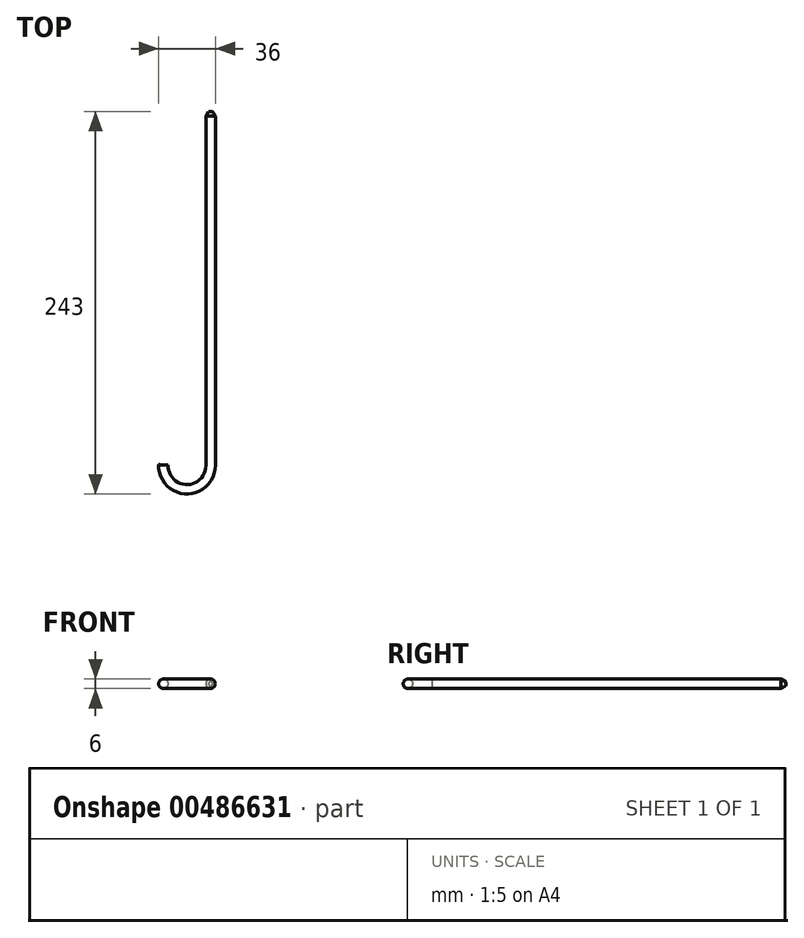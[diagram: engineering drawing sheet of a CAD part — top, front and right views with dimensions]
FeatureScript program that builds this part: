
annotation { "Feature Type Name" : "Feature", "Feature Type Description" : "" }
export const myFeature = defineFeature(function(context is Context, id is Id, definition is map)
    precondition{}
    {
        {
            var Q0;
            Q0=qCreatedBy(makeId("Top.planeOp"),FACE);
            var sketch = newSketch(context, id + "F0", { "sketchPlane" : qUnion([Q0])});
            skLineSegment(sketch, "E0", {"start": v(0, 0) * mm, "end": v(0, -225) * mm});
            skArc(sketch, "E1", {"start": v(0, -225) * mm, "mid": v(-15.28, -240) * mm, "end": v(-29.99, -224.45) * mm});
            skSolve(sketch);
        }
        {
            var Q0;
            Q0=qCreatedBy(makeId("Front.planeOp"),FACE);
            var sketch = newSketch(context, id + "F1", { "sketchPlane" : qUnion([Q0])});
            skCircle(sketch, "E2", {"center": v(0, 0) * mm, "radius": 3 * mm});
            skSolve(sketch);
        }
        {
            var Q0;
            Q0=makeQuery(id+"F1.imprint","IMPRINT",FACE,{"disambiguationData":[TD([[makeQuery(id+"F1.imprint","IMPRINT",EDGE,{"derivedFrom":sQuery(id+"F1.wireOp",EDGE,"E2")}),1.0]])]});
            var Q1;
            Q1=sQuery(id+"F0.wireOp",EDGE,"E0");
            var Q2;
            Q2=sQuery(id+"F0.wireOp",EDGE,"E1");
            sweep(context, id + "F2", {"profiles" : qUnion([Q0]), "path" : qUnion([Q1, Q2])});
        }
        {
            var Q0;
            Q0=makeQuery(id+"F2.opSweep","CAP_EDGE",EDGE,{"disambiguationData":[OSD([sQuery(id+"F0.wireOp",VERTEX,"E0.start"),sQuery(id+"F1.wireOp",EDGE,"E2")])],"isStart":true});
            chamfer(context, id + "F3", {"entities" : qUnion([Q0]), "chamferType" : ChamferType.OFFSET_ANGLE, "width" : 3 * mm, "oppositeDirection" : false, "angle" : 30 * degree, "tangentPropagation" : true});
        }
    });
